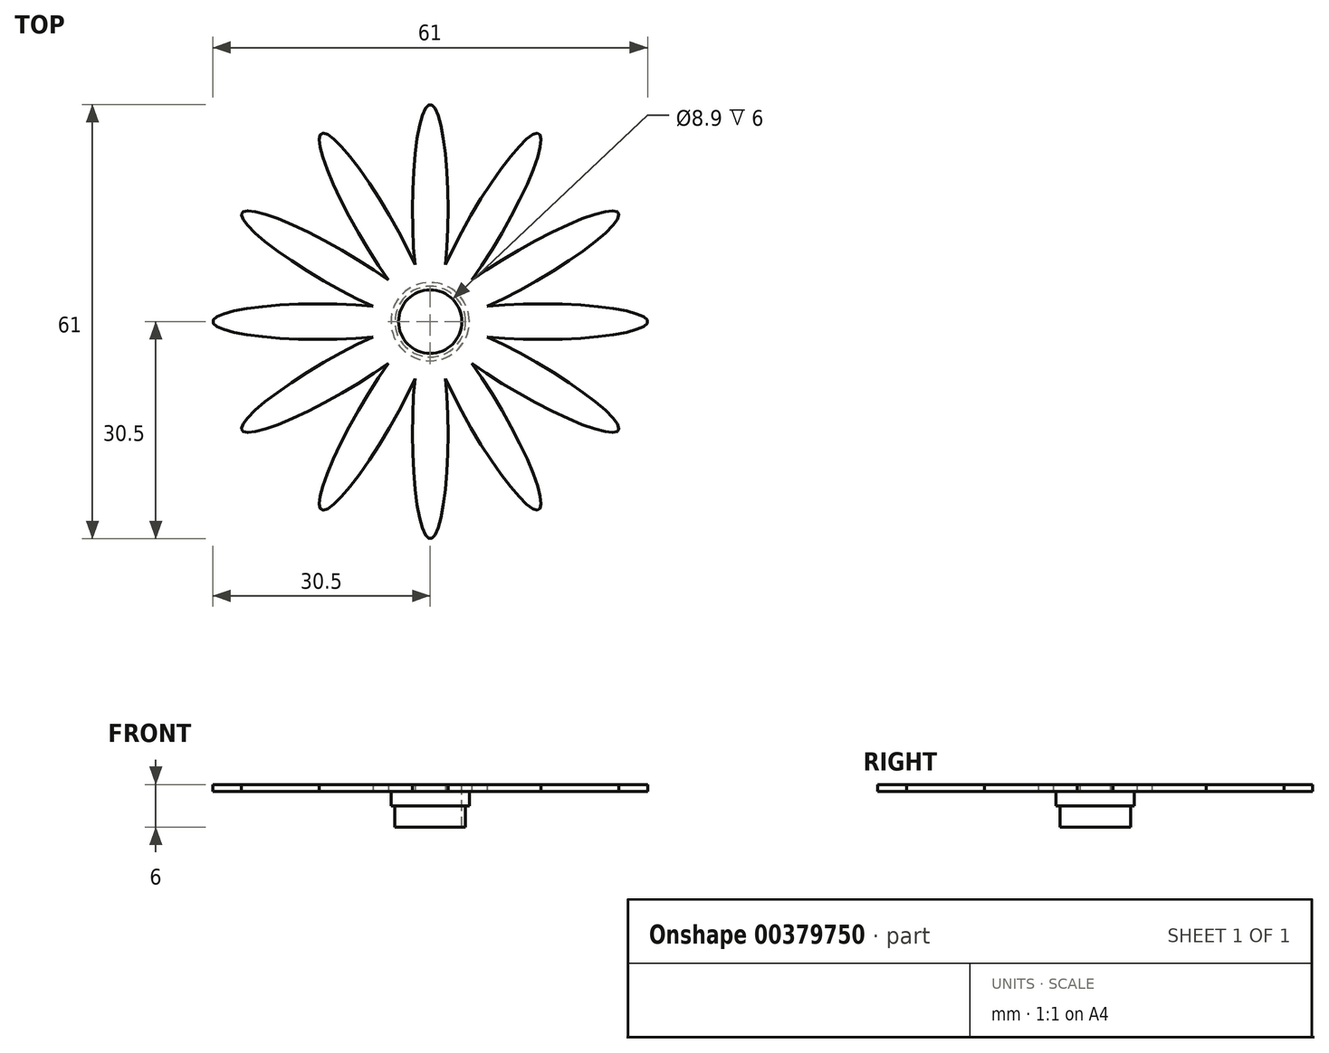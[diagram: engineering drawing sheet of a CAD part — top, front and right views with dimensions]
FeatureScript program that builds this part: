
annotation { "Feature Type Name" : "Feature", "Feature Type Description" : "" }
export const myFeature = defineFeature(function(context is Context, id is Id, definition is map)
    precondition{}
    {
        {
            var Q0;
            Q0=qCreatedBy(makeId("Top.planeOp"),FACE);
            var sketch = newSketch(context, id + "F0", { "sketchPlane" : qUnion([Q0])});
            skCircle(sketch, "E0", {"center": v(0, 0) * mm, "radius": 6 * mm});
            skEllipse(sketch, "E1", {"center": v(0, 15.66) * mm, "majorRadius": 14.85 * mm, "minorRadius": 2.5 * mm, "majorAxis": v(0, -1)});
            skSolve(sketch);
        }
        {
            var Q0;
            {var subQ0=sQuery(id+"F0.wireOp",EDGE,"E1");var subQ1=sQuery(id+"F0.wireOp",EDGE,"E0");var subQ2=makeQuery(id+"F0.imprint","INTERSECT",VERTEX,{"disambiguationData":[OD(0.0)],"derivedFrom":[subQ1,subQ0]});Q0=makeQuery(id+"F0.imprint","IMPRINT",FACE,{"disambiguationData":[TD([[makeQuery(id+"F0.imprint","IMPRINT",EDGE,{"disambiguationData":[TD([[subQ2,-1.0]])],"derivedFrom":subQ1}),1.0]])]});}
            var Q1;
            {var subQ0=sQuery(id+"F0.wireOp",EDGE,"E1");var subQ1=sQuery(id+"F0.wireOp",EDGE,"E0");var subQ2=makeQuery(id+"F0.imprint","INTERSECT",VERTEX,{"disambiguationData":[OD(0.0)],"derivedFrom":[subQ1,subQ0]});Q1=makeQuery(id+"F0.imprint","IMPRINT",FACE,{"disambiguationData":[TD([[makeQuery(id+"F0.imprint","IMPRINT",EDGE,{"disambiguationData":[TD([[subQ2,1.0]])],"derivedFrom":subQ1}),-1.0]])]});}
            var Q2;
            {var subQ0=sQuery(id+"F0.wireOp",EDGE,"E1");var subQ1=sQuery(id+"F0.wireOp",EDGE,"E0");var subQ2=makeQuery(id+"F0.imprint","INTERSECT",VERTEX,{"disambiguationData":[OD(0.0)],"derivedFrom":[subQ1,subQ0]});Q2=makeQuery(id+"F0.imprint","IMPRINT",FACE,{"disambiguationData":[TD([[makeQuery(id+"F0.imprint","IMPRINT",EDGE,{"disambiguationData":[TD([[subQ2,1.0]])],"derivedFrom":subQ1}),1.0]])]});}
            extrude(context, id + "F1", {"entities" : qUnion([Q0, Q1, Q2]), "depth" : 1 * mm, "offsetDistance" : 25 * mm});
        }
        {
            var Q0;
            Q0=qCreatedBy(makeId("Front.planeOp"),FACE);
            var sketch = newSketch(context, id + "F2", { "sketchPlane" : qUnion([Q0])});
            skLineSegment(sketch, "E2", {"start": v(0, 17.6) * mm, "end": v(0, 0) * mm, "construction": true});
            skSolve(sketch);
        }
        {
            var Q0;
            Q0=makeQuery(id+"F1.opExtrude","SWEPT_BODY",BODY,{"disambiguationData":[OSD([sQuery(id+"F0.wireOp",EDGE,"E0"),sQuery(id+"F0.wireOp",EDGE,"E1")])]});
            var Q1;
            Q1=sQuery(id+"F2.wireOp",EDGE,"E2");
            circularPattern(context, id + "F3", {"entities" : qUnion([Q0]), "axis" : qUnion([Q1]), "angle" : 360 * degree, "instanceCount" : 12, "equalSpace" : true, "computeTransformsWithoutBuiltin" : true});
        }
        {
            var Q0;
            Q0=qCreatedBy(makeId("Top.planeOp"),FACE);
            var sketch = newSketch(context, id + "F4", { "sketchPlane" : qUnion([Q0])});
            skCircle(sketch, "E3", {"center": v(0, 0) * mm, "radius": 4.95 * mm});
            skCircle(sketch, "E4", {"center": v(0, 0) * mm, "radius": 4.45 * mm});
            skCircle(sketch, "E5", {"center": v(0, 0) * mm, "radius": 5.5 * mm});
            skSolve(sketch);
        }
        {
            var Q0;
            Q0=makeQuery(id+"F4.imprint","IMPRINT",FACE,{"disambiguationData":[TD([[makeQuery(id+"F4.imprint","IMPRINT",EDGE,{"derivedFrom":sQuery(id+"F4.wireOp",EDGE,"E3")}),1.0]])]});
            extrude(context, id + "F5", {"entities" : qUnion([Q0]), "operationType" : NewBodyOperationType.ADD, "oppositeDirection" : true, "depth" : 5 * mm, "offsetDistance" : 25 * mm});
        }
        {
            var Q0;
            Q0=makeQuery(id+"F4.imprint","IMPRINT",FACE,{"disambiguationData":[TD([[makeQuery(id+"F4.imprint","IMPRINT",EDGE,{"derivedFrom":sQuery(id+"F4.wireOp",EDGE,"E3")}),-1.0]])]});
            extrude(context, id + "F6", {"entities" : qUnion([Q0]), "operationType" : NewBodyOperationType.ADD, "oppositeDirection" : true, "depth" : 2 * mm, "offsetDistance" : 25 * mm});
        }
        {
            var Q0;
            Q0=makeQuery(id+"F4.imprint","IMPRINT",FACE,{"disambiguationData":[TD([[makeQuery(id+"F4.imprint","IMPRINT",EDGE,{"derivedFrom":sQuery(id+"F4.wireOp",EDGE,"E4")}),1.0]])]});
            extrude(context, id + "F7", {"entities" : qUnion([Q0]), "operationType" : NewBodyOperationType.REMOVE, "depth" : 2 * mm, "offsetDistance" : 25 * mm});
        }
    });
